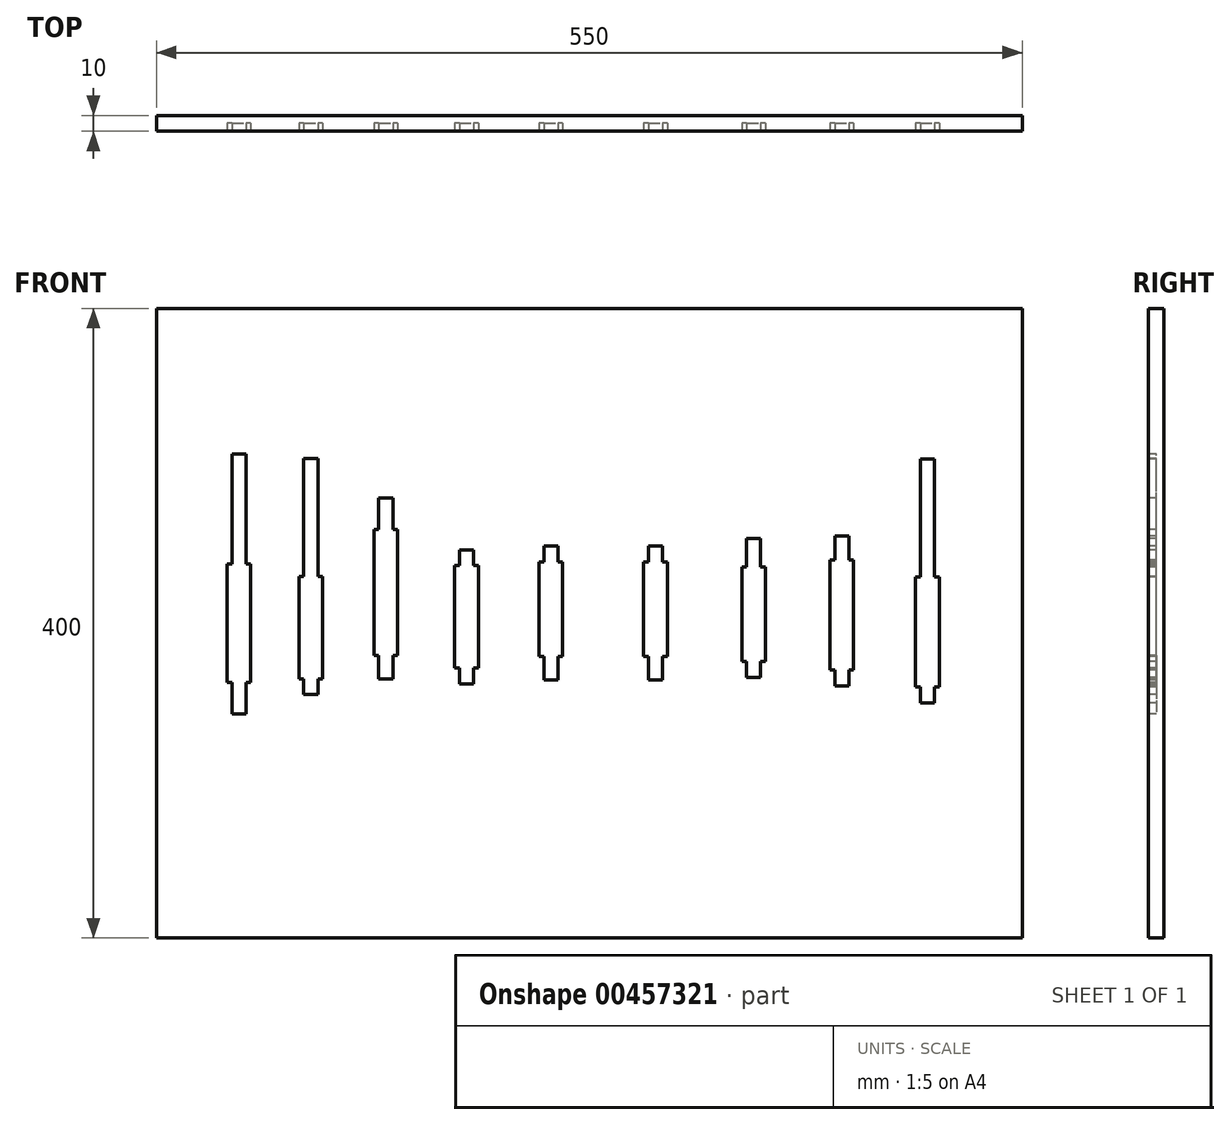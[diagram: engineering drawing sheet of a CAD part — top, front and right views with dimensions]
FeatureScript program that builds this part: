
annotation { "Feature Type Name" : "Feature", "Feature Type Description" : "" }
export const myFeature = defineFeature(function(context is Context, id is Id, definition is map)
    precondition{}
    {
        {
            var Q0;
            Q0=qCreatedBy(makeId("Front.planeOp"),FACE);
            var sketch = newSketch(context, id + "F0", { "sketchPlane" : qUnion([Q0])});
            skLineSegment(sketch, "E0.bottom", {"start": v(275, -200) * mm, "end": v(-275, -200) * mm});
            skLineSegment(sketch, "E0.top", {"start": v(275, 200) * mm, "end": v(-275, 200) * mm});
            skLineSegment(sketch, "E0.left", {"start": v(275, -200) * mm, "end": v(275, 200) * mm});
            skLineSegment(sketch, "E0.right", {"start": v(-275, -200) * mm, "end": v(-275, 200) * mm});
            skPoint(sketch, "E0.middle", {"position": v(0, 0) * mm});
            skSolve(sketch);
        }
        {
            var Q0;
            Q0=makeQuery(id+"F0.imprint","IMPRINT",FACE,{"disambiguationData":[TD([[makeQuery(id+"F0.imprint","IMPRINT",EDGE,{"derivedFrom":sQuery(id+"F0.wireOp",EDGE,"E0.bottom")}),-1.0]])]});
            extrude(context, id + "F1", {"entities" : qUnion([Q0]), "depth" : 10 * mm});
        }
        {
            var Q0;
            Q0=makeQuery(id+"F1.opExtrude","CAP_FACE",FACE,{"disambiguationData":[OSD([sQuery(id+"F0.wireOp",EDGE,"E0.bottom"),sQuery(id+"F0.wireOp",EDGE,"E0.top"),sQuery(id+"F0.wireOp",EDGE,"E0.left"),sQuery(id+"F0.wireOp",EDGE,"E0.right")])],"isStart":false});
            var sketch = newSketch(context, id + "F2", { "sketchPlane" : qUnion([Q0])});
            skLineSegment(sketch, "E1.bottom", {"start": v(-215.01, -37.5) * mm, "end": v(-230.01, -37.5) * mm});
            skLineSegment(sketch, "E1.top", {"start": v(-215.01, 37.5) * mm, "end": v(-230.01, 37.5) * mm});
            skLineSegment(sketch, "E1.left", {"start": v(-215.01, -37.5) * mm, "end": v(-215.01, 37.5) * mm});
            skLineSegment(sketch, "E1.right", {"start": v(-230.01, -37.5) * mm, "end": v(-230.01, 37.5) * mm});
            skPoint(sketch, "E1.middle", {"position": v(-222.51, 0) * mm});
            skLineSegment(sketch, "E2.bottom", {"start": v(-227.01, 37.5) * mm, "end": v(-218.01, 37.5) * mm});
            skLineSegment(sketch, "E2.top", {"start": v(-227.01, 107.5) * mm, "end": v(-218.01, 107.5) * mm});
            skLineSegment(sketch, "E2.left", {"start": v(-227.01, 37.5) * mm, "end": v(-227.01, 107.5) * mm});
            skLineSegment(sketch, "E2.right", {"start": v(-218.01, 37.5) * mm, "end": v(-218.01, 107.5) * mm});
            skLineSegment(sketch, "E3.bottom", {"start": v(-227.01, -37.5) * mm, "end": v(-218.01, -37.5) * mm});
            skLineSegment(sketch, "E3.top", {"start": v(-227.01, -57.5) * mm, "end": v(-218.01, -57.5) * mm});
            skLineSegment(sketch, "E3.left", {"start": v(-227.01, -37.5) * mm, "end": v(-227.01, -57.5) * mm});
            skLineSegment(sketch, "E3.right", {"start": v(-218.01, -37.5) * mm, "end": v(-218.01, -57.5) * mm});
            skLineSegment(sketch, "E4.bottom", {"start": v(222.22, -40.56) * mm, "end": v(207.22, -40.56) * mm});
            skLineSegment(sketch, "E4.top", {"start": v(222.22, 29.44) * mm, "end": v(207.22, 29.44) * mm});
            skLineSegment(sketch, "E4.left", {"start": v(222.22, -40.56) * mm, "end": v(222.22, 29.44) * mm});
            skLineSegment(sketch, "E4.right", {"start": v(207.22, -40.56) * mm, "end": v(207.22, 29.44) * mm});
            skLineSegment(sketch, "E5.bottom", {"start": v(210.22, 29.44) * mm, "end": v(219.22, 29.44) * mm});
            skLineSegment(sketch, "E5.top", {"start": v(210.22, 104.44) * mm, "end": v(219.22, 104.44) * mm});
            skLineSegment(sketch, "E5.left", {"start": v(210.22, 29.44) * mm, "end": v(210.22, 104.44) * mm});
            skLineSegment(sketch, "E5.right", {"start": v(219.22, 29.44) * mm, "end": v(219.22, 104.44) * mm});
            skLineSegment(sketch, "E6.top", {"start": v(210.22, -50.56) * mm, "end": v(219.22, -50.56) * mm});
            skLineSegment(sketch, "E6.left", {"start": v(210.22, -40.56) * mm, "end": v(210.22, -50.56) * mm});
            skLineSegment(sketch, "E6.right", {"start": v(219.22, -40.56) * mm, "end": v(219.22, -50.56) * mm});
            skLineSegment(sketch, "E7", {"start": v(210.22, -40.56) * mm, "end": v(219.22, -40.56) * mm});
            skLineSegment(sketch, "E8.bottom", {"start": v(-169.43, -35.36) * mm, "end": v(-184.43, -35.36) * mm});
            skLineSegment(sketch, "E8.top", {"start": v(-169.43, 29.64) * mm, "end": v(-184.43, 29.64) * mm});
            skLineSegment(sketch, "E8.left", {"start": v(-169.43, -35.36) * mm, "end": v(-169.43, 29.64) * mm});
            skLineSegment(sketch, "E8.right", {"start": v(-184.43, -35.36) * mm, "end": v(-184.43, 29.64) * mm});
            skLineSegment(sketch, "E9.top", {"start": v(-181.43, 104.64) * mm, "end": v(-172.43, 104.64) * mm});
            skLineSegment(sketch, "E9.left", {"start": v(-181.43, 29.64) * mm, "end": v(-181.43, 104.64) * mm});
            skLineSegment(sketch, "E9.right", {"start": v(-172.43, 29.64) * mm, "end": v(-172.43, 104.64) * mm});
            skLineSegment(sketch, "E10.top", {"start": v(-181.43, -45.36) * mm, "end": v(-172.43, -45.36) * mm});
            skLineSegment(sketch, "E10.left", {"start": v(-181.43, -35.36) * mm, "end": v(-181.43, -45.36) * mm});
            skLineSegment(sketch, "E10.right", {"start": v(-172.43, -35.36) * mm, "end": v(-172.43, -45.36) * mm});
            skLineSegment(sketch, "E11", {"start": v(-181.43, -35.36) * mm, "end": v(-172.43, -35.36) * mm});
            skLineSegment(sketch, "E12", {"start": v(-181.43, 29.64) * mm, "end": v(-172.43, 29.64) * mm});
            skLineSegment(sketch, "E13.bottom", {"start": v(-121.8, -20.36) * mm, "end": v(-136.8, -20.36) * mm});
            skLineSegment(sketch, "E13.top", {"start": v(-121.8, 59.64) * mm, "end": v(-136.8, 59.64) * mm});
            skLineSegment(sketch, "E13.left", {"start": v(-121.8, -20.36) * mm, "end": v(-121.8, 59.64) * mm});
            skLineSegment(sketch, "E13.right", {"start": v(-136.8, -20.36) * mm, "end": v(-136.8, 59.64) * mm});
            skLineSegment(sketch, "E14.top", {"start": v(-133.8, 79.64) * mm, "end": v(-124.8, 79.64) * mm});
            skLineSegment(sketch, "E14.left", {"start": v(-133.8, 59.64) * mm, "end": v(-133.8, 79.64) * mm});
            skLineSegment(sketch, "E14.right", {"start": v(-124.8, 59.64) * mm, "end": v(-124.8, 79.64) * mm});
            skLineSegment(sketch, "E15.top", {"start": v(-133.8, -35.36) * mm, "end": v(-124.8, -35.36) * mm});
            skLineSegment(sketch, "E15.left", {"start": v(-133.8, -20.36) * mm, "end": v(-133.8, -35.36) * mm});
            skLineSegment(sketch, "E15.right", {"start": v(-124.8, -20.36) * mm, "end": v(-124.8, -35.36) * mm});
            skLineSegment(sketch, "E16", {"start": v(-133.8, -20.36) * mm, "end": v(-124.8, -20.36) * mm});
            skLineSegment(sketch, "E17", {"start": v(-133.8, 59.64) * mm, "end": v(-124.8, 59.64) * mm});
            skLineSegment(sketch, "E18.bottom", {"start": v(-70.53, -28.5) * mm, "end": v(-85.53, -28.5) * mm});
            skLineSegment(sketch, "E18.top", {"start": v(-70.53, 36.5) * mm, "end": v(-85.53, 36.5) * mm});
            skLineSegment(sketch, "E18.left", {"start": v(-70.53, -28.5) * mm, "end": v(-70.53, 36.5) * mm});
            skLineSegment(sketch, "E18.right", {"start": v(-85.53, -28.5) * mm, "end": v(-85.53, 36.5) * mm});
            skLineSegment(sketch, "E19.top", {"start": v(-82.53, 46.5) * mm, "end": v(-73.53, 46.5) * mm});
            skLineSegment(sketch, "E19.left", {"start": v(-82.53, 36.5) * mm, "end": v(-82.53, 46.5) * mm});
            skLineSegment(sketch, "E19.right", {"start": v(-73.53, 36.5) * mm, "end": v(-73.53, 46.5) * mm});
            skLineSegment(sketch, "E20.top", {"start": v(-82.53, -38.5) * mm, "end": v(-73.53, -38.5) * mm});
            skLineSegment(sketch, "E20.left", {"start": v(-82.53, -28.5) * mm, "end": v(-82.53, -38.5) * mm});
            skLineSegment(sketch, "E20.right", {"start": v(-73.53, -28.5) * mm, "end": v(-73.53, -38.5) * mm});
            skLineSegment(sketch, "E21", {"start": v(-82.53, -28.5) * mm, "end": v(-73.53, -28.5) * mm});
            skLineSegment(sketch, "E22", {"start": v(-82.53, 36.5) * mm, "end": v(-73.53, 36.5) * mm});
            skLineSegment(sketch, "E23.bottom", {"start": v(-16.9, -21.07) * mm, "end": v(-31.9, -21.07) * mm});
            skLineSegment(sketch, "E23.top", {"start": v(-16.9, 38.93) * mm, "end": v(-31.9, 38.93) * mm});
            skLineSegment(sketch, "E23.left", {"start": v(-16.9, -21.07) * mm, "end": v(-16.9, 38.93) * mm});
            skLineSegment(sketch, "E23.right", {"start": v(-31.9, -21.07) * mm, "end": v(-31.9, 38.93) * mm});
            skLineSegment(sketch, "E24.top", {"start": v(-28.9, 48.93) * mm, "end": v(-19.9, 48.93) * mm});
            skLineSegment(sketch, "E24.left", {"start": v(-28.9, 38.93) * mm, "end": v(-28.9, 48.93) * mm});
            skLineSegment(sketch, "E24.right", {"start": v(-19.9, 38.93) * mm, "end": v(-19.9, 48.93) * mm});
            skLineSegment(sketch, "E25.top", {"start": v(-28.9, -36.07) * mm, "end": v(-19.9, -36.07) * mm});
            skLineSegment(sketch, "E25.left", {"start": v(-28.9, -21.07) * mm, "end": v(-28.9, -36.07) * mm});
            skLineSegment(sketch, "E25.right", {"start": v(-19.9, -21.07) * mm, "end": v(-19.9, -36.07) * mm});
            skLineSegment(sketch, "E26", {"start": v(-28.9, -21.07) * mm, "end": v(-19.9, -21.07) * mm});
            skLineSegment(sketch, "E27", {"start": v(-28.9, 38.93) * mm, "end": v(-19.9, 38.93) * mm});
            skLineSegment(sketch, "E28.bottom", {"start": v(49.5, -21.07) * mm, "end": v(34.5, -21.07) * mm});
            skLineSegment(sketch, "E28.top", {"start": v(49.5, 38.93) * mm, "end": v(34.5, 38.93) * mm});
            skLineSegment(sketch, "E28.left", {"start": v(49.5, -21.07) * mm, "end": v(49.5, 38.93) * mm});
            skLineSegment(sketch, "E28.right", {"start": v(34.5, -21.07) * mm, "end": v(34.5, 38.93) * mm});
            skLineSegment(sketch, "E29.top", {"start": v(37.5, 48.93) * mm, "end": v(46.5, 48.93) * mm});
            skLineSegment(sketch, "E29.left", {"start": v(37.5, 38.93) * mm, "end": v(37.5, 48.93) * mm});
            skLineSegment(sketch, "E29.right", {"start": v(46.5, 38.93) * mm, "end": v(46.5, 48.93) * mm});
            skLineSegment(sketch, "E30.top", {"start": v(37.5, -36.07) * mm, "end": v(46.5, -36.07) * mm});
            skLineSegment(sketch, "E30.left", {"start": v(37.5, -21.07) * mm, "end": v(37.5, -36.07) * mm});
            skLineSegment(sketch, "E30.right", {"start": v(46.5, -21.07) * mm, "end": v(46.5, -36.07) * mm});
            skLineSegment(sketch, "E31", {"start": v(37.5, -21.07) * mm, "end": v(46.5, -21.07) * mm});
            skLineSegment(sketch, "E32", {"start": v(37.5, 38.93) * mm, "end": v(46.5, 38.93) * mm});
            skLineSegment(sketch, "E33.bottom", {"start": v(111.83, -24.36) * mm, "end": v(96.83, -24.36) * mm});
            skLineSegment(sketch, "E33.top", {"start": v(111.83, 35.64) * mm, "end": v(96.83, 35.64) * mm});
            skLineSegment(sketch, "E33.left", {"start": v(111.83, -24.36) * mm, "end": v(111.83, 35.64) * mm});
            skLineSegment(sketch, "E33.right", {"start": v(96.83, -24.36) * mm, "end": v(96.83, 35.64) * mm});
            skLineSegment(sketch, "E34.top", {"start": v(99.83, 53.64) * mm, "end": v(108.83, 53.64) * mm});
            skLineSegment(sketch, "E34.left", {"start": v(99.83, 35.64) * mm, "end": v(99.83, 53.64) * mm});
            skLineSegment(sketch, "E34.right", {"start": v(108.83, 35.64) * mm, "end": v(108.83, 53.64) * mm});
            skLineSegment(sketch, "E35.top", {"start": v(99.83, -34.36) * mm, "end": v(108.83, -34.36) * mm});
            skLineSegment(sketch, "E35.left", {"start": v(99.83, -24.36) * mm, "end": v(99.83, -34.36) * mm});
            skLineSegment(sketch, "E35.right", {"start": v(108.83, -24.36) * mm, "end": v(108.83, -34.36) * mm});
            skLineSegment(sketch, "E36", {"start": v(99.83, -24.36) * mm, "end": v(108.83, -24.36) * mm});
            skLineSegment(sketch, "E37", {"start": v(99.83, 35.64) * mm, "end": v(108.83, 35.64) * mm});
            skLineSegment(sketch, "E38.bottom", {"start": v(167.84, -29.71) * mm, "end": v(152.84, -29.71) * mm});
            skLineSegment(sketch, "E38.top", {"start": v(167.84, 40.29) * mm, "end": v(152.84, 40.29) * mm});
            skLineSegment(sketch, "E38.left", {"start": v(167.84, -29.71) * mm, "end": v(167.84, 40.29) * mm});
            skLineSegment(sketch, "E38.right", {"start": v(152.84, -29.71) * mm, "end": v(152.84, 40.29) * mm});
            skLineSegment(sketch, "E39.top", {"start": v(155.84, 55.29) * mm, "end": v(164.84, 55.29) * mm});
            skLineSegment(sketch, "E39.left", {"start": v(155.84, 40.29) * mm, "end": v(155.84, 55.29) * mm});
            skLineSegment(sketch, "E39.right", {"start": v(164.84, 40.29) * mm, "end": v(164.84, 55.29) * mm});
            skLineSegment(sketch, "E40.top", {"start": v(155.84, -39.71) * mm, "end": v(164.84, -39.71) * mm});
            skLineSegment(sketch, "E40.left", {"start": v(155.84, -29.71) * mm, "end": v(155.84, -39.71) * mm});
            skLineSegment(sketch, "E40.right", {"start": v(164.84, -29.71) * mm, "end": v(164.84, -39.71) * mm});
            skLineSegment(sketch, "E41", {"start": v(155.84, -29.71) * mm, "end": v(164.84, -29.71) * mm});
            skLineSegment(sketch, "E42", {"start": v(155.84, 40.29) * mm, "end": v(164.84, 40.29) * mm});
            skSolve(sketch);
        }
        {
            var Q0;
            Q0 = qSketchRegion(id + "F2", true);
            extrude(context, id + "F3", {"entities" : qUnion([Q0]), "operationType" : NewBodyOperationType.REMOVE, "oppositeDirection" : true, "depth" : 5 * mm});
        }
    });
